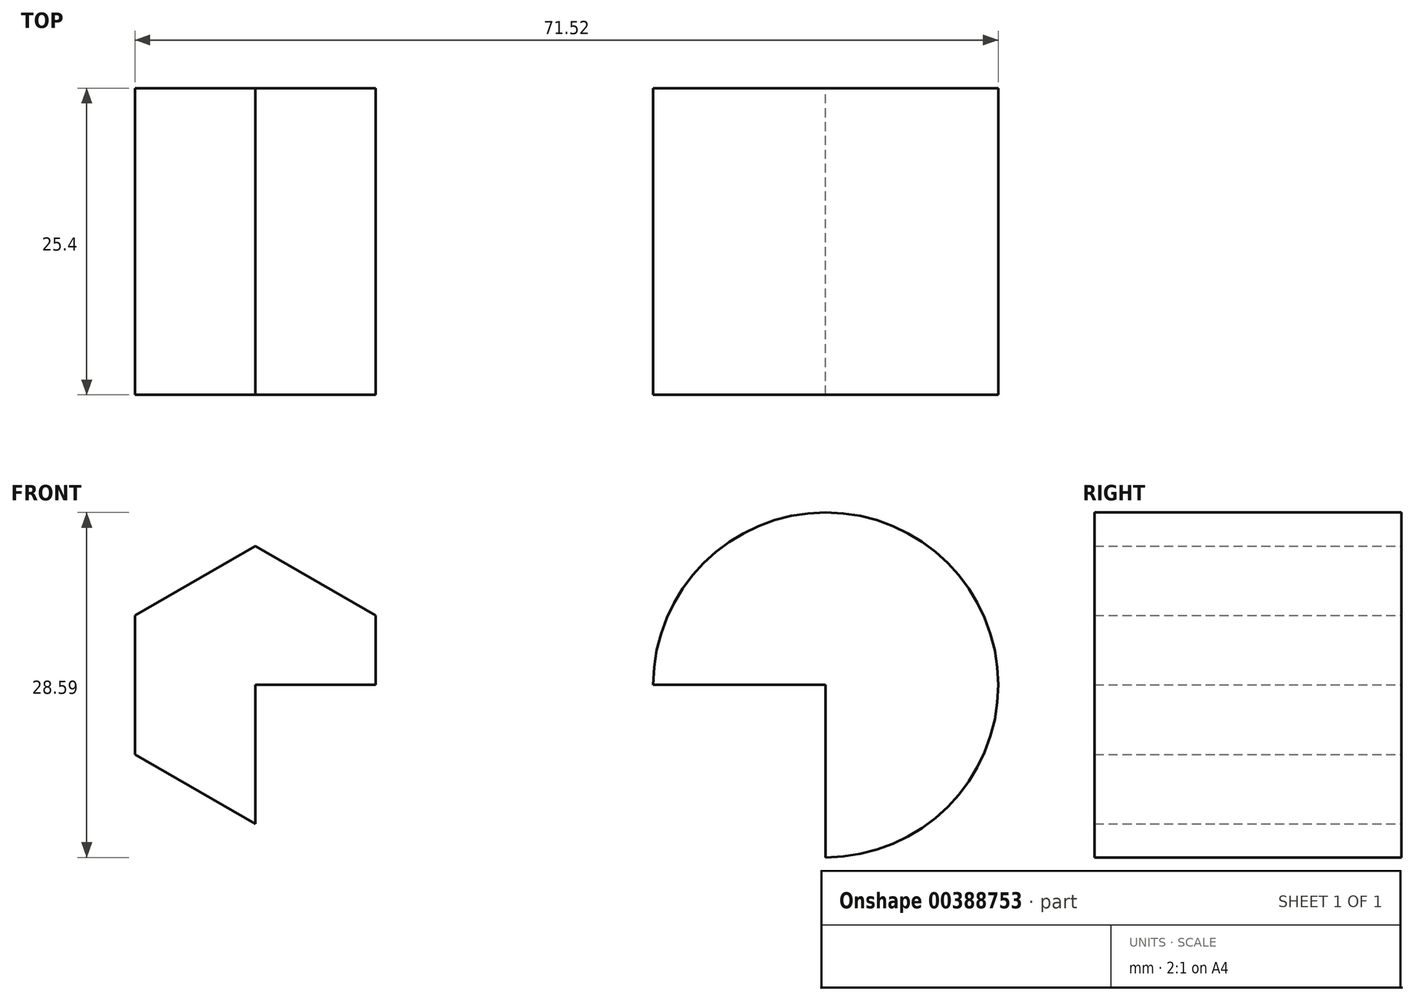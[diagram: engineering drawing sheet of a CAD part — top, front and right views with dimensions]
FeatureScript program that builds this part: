
annotation { "Feature Type Name" : "Feature", "Feature Type Description" : "" }
export const myFeature = defineFeature(function(context is Context, id is Id, definition is map)
    precondition{}
    {
        {
            var Q0;
            Q0=qCreatedBy(makeId("Front.planeOp"),FACE);
            var sketch = newSketch(context, id + "F0", { "sketchPlane" : qUnion([Q0])});
            skLineSegment(sketch, "E0.bottom", {"start": v(0, 0) * mm, "end": v(-47.26, 0) * mm});
            skLineSegment(sketch, "E0.top", {"start": v(0, 33.88) * mm, "end": v(-47.26, 33.88) * mm});
            skLineSegment(sketch, "E0.left", {"start": v(0, 0) * mm, "end": v(0, 33.88) * mm});
            skLineSegment(sketch, "E0.right", {"start": v(-47.26, 0) * mm, "end": v(-47.26, 33.88) * mm});
            skCircle(sketch, "E1", {"center": v(0, 33.88) * mm, "radius": 14.3 * mm});
            skCircle(sketch, "E2", {"center": v(-47.26, 0) * mm, "radius": 13.61 * mm});
            skCircle(sketch, "E3.cCircle", {"center": v(-47.26, 33.88) * mm, "radius": 9.97 * mm, "construction": true});
            skLineSegment(sketch, "E3.0", {"start": v(-57.23, 28.12) * mm, "end": v(-57.23, 39.64) * mm});
            skLineSegment(sketch, "E3.1", {"start": v(-57.23, 39.64) * mm, "end": v(-47.26, 45.4) * mm});
            skLineSegment(sketch, "E3.2", {"start": v(-47.26, 45.4) * mm, "end": v(-37.28, 39.64) * mm});
            skLineSegment(sketch, "E3.3", {"start": v(-37.28, 39.64) * mm, "end": v(-37.28, 28.12) * mm});
            skLineSegment(sketch, "E3.4", {"start": v(-37.28, 28.12) * mm, "end": v(-47.26, 22.37) * mm});
            skLineSegment(sketch, "E3.5", {"start": v(-47.26, 22.37) * mm, "end": v(-57.23, 28.12) * mm});
            skPoint(sketch, "E3.0.midPoint", {"position": v(-57.23, 33.88) * mm});
            skLineSegment(sketch, "E4", {"start": v(-47.26, 0) * mm, "end": v(-47.26, -13.61) * mm});
            skLineSegment(sketch, "E5", {"start": v(14.3, 33.92) * mm, "end": v(36.85, 33.92) * mm});
            skLineSegment(sketch, "E6.bottom", {"start": v(14.88, 19.05) * mm, "end": v(36.65, 19.05) * mm});
            skLineSegment(sketch, "E6.top", {"start": v(14.88, 5.2) * mm, "end": v(36.65, 5.2) * mm});
            skLineSegment(sketch, "E6.left", {"start": v(14.88, 19.05) * mm, "end": v(14.88, 5.2) * mm});
            skLineSegment(sketch, "E6.right", {"start": v(36.65, 19.05) * mm, "end": v(36.65, 5.2) * mm});
            skSolve(sketch);
        }
        {
            var Q0;
            Q0=makeQuery(id+"F0.imprint","IMPRINT",FACE,{"disambiguationData":[TD([[makeQuery(id+"F0.imprint","IMPRINT",EDGE,{"derivedFrom":sQuery(id+"F0.wireOp",EDGE,"E3.0")}),-1.0]])]});
            var Q1;
            {var subQ0=sQuery(id+"F0.wireOp",EDGE,"E0.left");var subQ1=sQuery(id+"F0.wireOp",EDGE,"E0.top");var subQ2=makeQuery(id+"F0.imprint","INTERSECT",VERTEX,{"derivedFrom":[subQ1,subQ0]});Q1=makeQuery(id+"F0.imprint","IMPRINT",FACE,{"disambiguationData":[TD([[makeQuery(id+"F0.imprint","IMPRINT",EDGE,{"disambiguationData":[TD([[subQ2,-1.0]])],"derivedFrom":subQ1}),-1.0]])]});}
            extrude(context, id + "F1", {"entities" : qUnion([Q0, Q1]), "endBound" : BoundingType.SYMMETRIC, "depth" : 25.4 * mm});
        }
    });
